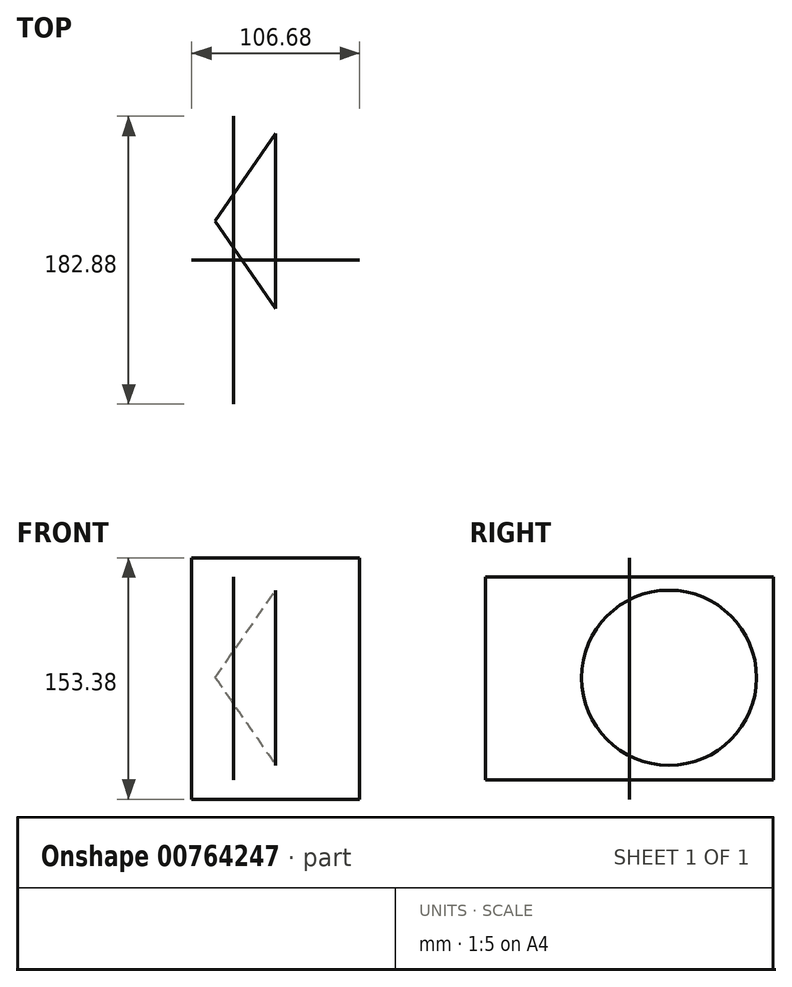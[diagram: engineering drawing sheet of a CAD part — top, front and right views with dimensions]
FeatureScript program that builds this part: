
annotation { "Feature Type Name" : "Feature", "Feature Type Description" : "" }
export const myFeature = defineFeature(function(context is Context, id is Id, definition is map)
    precondition{}
    {
        {
            var Q0;
            Q0=qCreatedBy(makeId("Front.planeOp"),FACE);
            var sketch = newSketch(context, id + "F0", { "sketchPlane" : qUnion([Q0])});
            skLineSegment(sketch, "E0", {"start": v(0, 55.58) * mm, "end": v(-38.44, 0) * mm});
            skLineSegment(sketch, "E1", {"start": v(-38.44, 0) * mm, "end": v(0, 0) * mm});
            skSolve(sketch);
        }
        {
            var Q0;
            Q0 = qSketchRegion(id + "F0", true);
            var Q1;
            Q1=sQuery(id+"F0.wireOp",EDGE,"E0");
            var Q2;
            Q2=sQuery(id+"F0.wireOp",EDGE,"E1");
            revolve(context, id + "F1", {"bodyType" : ToolBodyType.SURFACE, "surfaceOperationType" : NewSurfaceOperationType.NEW, "entities" : qUnion([Q0]), "surfaceEntities" : qUnion([Q1]), "axis" : qUnion([Q2]), "revolveType" : RevolveType.FULL});
        }
        {
            var Q0;
            Q0=qCreatedBy(makeId("Right.planeOp"),FACE);
            var sketch = newSketch(context, id + "F2", { "sketchPlane" : qUnion([Q0])});
            skLineSegment(sketch, "E2", {"start": v(-24.98, 76.23) * mm, "end": v(-24.98, -77.15) * mm});
            skSolve(sketch);
        }
        {
            var Q0;
            Q0=sQuery(id+"F2.wireOp",EDGE,"E2");
            extrude(context, id + "F3", {"bodyType" : ToolBodyType.SURFACE, "surfaceEntities" : qUnion([Q0]), "endBound" : BoundingType.SYMMETRIC, "oppositeDirection" : true, "depth" : 106.68 * mm, "offsetDistance" : 25.4 * mm});
        }
        {
            var Q0;
            Q0=makeQuery(id+"F3.opExtrude","SWEPT_FACE",FACE,{"disambiguationData":[OSD([sQuery(id+"F2.wireOp",EDGE,"E2")])]});
            var sketch = newSketch(context, id + "F4", { "sketchPlane" : qUnion([Q0])});
            skLineSegment(sketch, "E3", {"start": v(26.81, 64.02) * mm, "end": v(26.81, -64.75) * mm});
            skSolve(sketch);
        }
        {
            var Q0;
            Q0 = qSketchRegion(id + "F4", true);
            var Q1;
            Q1=sQuery(id+"F4.wireOp",EDGE,"E3");
            extrude(context, id + "F5", {"entities" : qUnion([Q0]), "bodyType" : ToolBodyType.SURFACE, "surfaceEntities" : qUnion([Q1]), "endBound" : BoundingType.SYMMETRIC, "depth" : 182.88 * mm, "offsetDistance" : 25.4 * mm});
        }
    });
